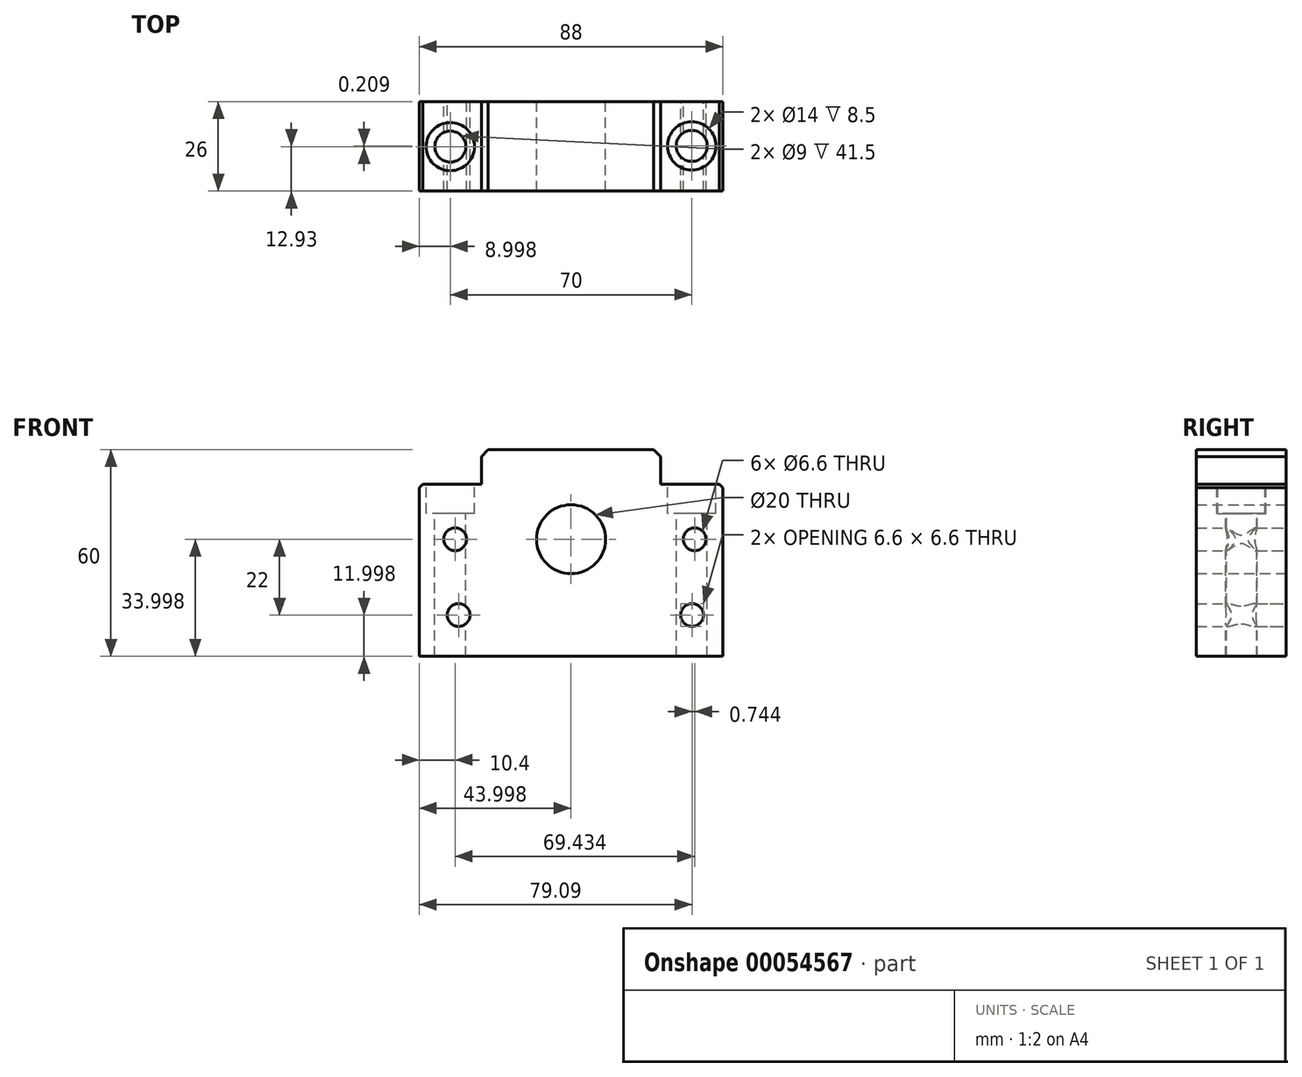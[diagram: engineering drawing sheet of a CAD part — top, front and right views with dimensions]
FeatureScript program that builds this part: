
annotation { "Feature Type Name" : "Feature", "Feature Type Description" : "" }
export const myFeature = defineFeature(function(context is Context, id is Id, definition is map)
    precondition{}
    {
        {
            var Q0;
            Q0=qCreatedBy(makeId("Front.planeOp"),FACE);
            var sketch = newSketch(context, id + "F0", { "sketchPlane" : qUnion([Q0])});
            skLineSegment(sketch, "E0.bottom", {"start": v(-44.44, 23.42) * mm, "end": v(-26.44, 23.42) * mm});
            skLineSegment(sketch, "E0.top", {"start": v(-44.44, -26.58) * mm, "end": v(43.56, -26.58) * mm});
            skLineSegment(sketch, "E0.left", {"start": v(-44.44, 23.42) * mm, "end": v(-44.44, -26.58) * mm});
            skLineSegment(sketch, "E0.right", {"start": v(43.56, 23.42) * mm, "end": v(43.56, -26.58) * mm});
            skLineSegment(sketch, "E1.bottom", {"start": v(-26.44, 33.42) * mm, "end": v(25.56, 33.42) * mm});
            skLineSegment(sketch, "E1.left", {"start": v(-26.44, 33.42) * mm, "end": v(-26.44, 23.42) * mm});
            skLineSegment(sketch, "E1.right", {"start": v(25.56, 33.42) * mm, "end": v(25.56, 23.42) * mm});
            skLineSegment(sketch, "E2.trimOffspring", {"start": v(25.56, 23.42) * mm, "end": v(43.56, 23.42) * mm});
            skCircle(sketch, "E3", {"center": v(-0.44, 7.42) * mm, "radius": 10 * mm});
            skCircle(sketch, "E4", {"center": v(-34.04, 7.42) * mm, "radius": 3.3 * mm});
            skCircle(sketch, "E5", {"center": v(-33.05, -14.58) * mm, "radius": 3.3 * mm});
            skCircle(sketch, "E6", {"center": v(34.65, -14.58) * mm, "radius": 3.3 * mm});
            skCircle(sketch, "E7", {"center": v(35.4, 7.42) * mm, "radius": 3.3 * mm});
            skSolve(sketch);
        }
        {
            var Q0;
            Q0 = qSketchRegion(id + "F0", true);
            extrude(context, id + "F1", {"entities" : qUnion([Q0]), "depth" : 26 * mm});
        }
        {
            var Q0;
            Q0=makeQuery(id+"F1.opExtrude","SWEPT_EDGE",EDGE,{"disambiguationData":[OSD([sQuery(id+"F0.wireOp",EDGE,"E0.bottom"),sQuery(id+"F0.wireOp",EDGE,"E0.left")])]});
            var Q1;
            Q1=makeQuery(id+"F1.opExtrude","SWEPT_EDGE",EDGE,{"disambiguationData":[OSD([sQuery(id+"F0.wireOp",EDGE,"E0.right"),sQuery(id+"F0.wireOp",EDGE,"E2.trimOffspring")])]});
            chamfer(context, id + "F2", {"entities" : qUnion([Q0, Q1]), "width" : 1 * mm, "tangentPropagation" : true});
        }
        {
            var Q0;
            Q0=makeQuery(id+"F1.opExtrude","SWEPT_EDGE",EDGE,{"disambiguationData":[OSD([sQuery(id+"F0.wireOp",EDGE,"E1.bottom"),sQuery(id+"F0.wireOp",EDGE,"E1.left")])]});
            var Q1;
            Q1=makeQuery(id+"F1.opExtrude","SWEPT_EDGE",EDGE,{"disambiguationData":[OSD([sQuery(id+"F0.wireOp",EDGE,"E1.bottom"),sQuery(id+"F0.wireOp",EDGE,"E1.right")])]});
            chamfer(context, id + "F3", {"entities" : qUnion([Q0, Q1]), "width" : 2 * mm, "tangentPropagation" : true});
        }
        {
            var Q0;
            Q0=makeQuery(id+"F1.opExtrude","SWEPT_FACE",FACE,{"disambiguationData":[OSD([sQuery(id+"F0.wireOp",EDGE,"E0.bottom")])]});
            var sketch = newSketch(context, id + "F4", { "sketchPlane" : qUnion([Q0])});
            skCircle(sketch, "E8", {"center": v(-35.44, -13.07) * mm, "radius": 4.5 * mm});
            skCircle(sketch, "E9", {"center": v(34.56, -12.86) * mm, "radius": 4.5 * mm});
            skCircle(sketch, "E10", {"center": v(-35.44, -13.07) * mm, "radius": 7 * mm});
            skCircle(sketch, "E11", {"center": v(34.56, -12.86) * mm, "radius": 7 * mm});
            skSolve(sketch);
        }
        {
            var Q0;
            Q0 = qSketchRegion(id + "F4", true);
            extrude(context, id + "F5", {"entities" : qUnion([Q0]), "operationType" : NewBodyOperationType.REMOVE, "oppositeDirection" : true, "depth" : 8.5 * mm});
        }
        {
            var Q0;
            Q0=makeQuery(id+"F4.imprint","IMPRINT",FACE,{"disambiguationData":[TD([[makeQuery(id+"F4.imprint","IMPRINT",EDGE,{"derivedFrom":sQuery(id+"F4.wireOp",EDGE,"E8")}),1.0]])]});
            var Q1;
            Q1=makeQuery(id+"F4.imprint","IMPRINT",FACE,{"disambiguationData":[TD([[makeQuery(id+"F4.imprint","IMPRINT",EDGE,{"derivedFrom":sQuery(id+"F4.wireOp",EDGE,"E9")}),1.0]])]});
            extrude(context, id + "F6", {"entities" : qUnion([Q0, Q1]), "operationType" : NewBodyOperationType.REMOVE, "endBound" : BoundingType.THROUGH_ALL, "oppositeDirection" : true, "depth" : 25 * mm});
        }
    });
